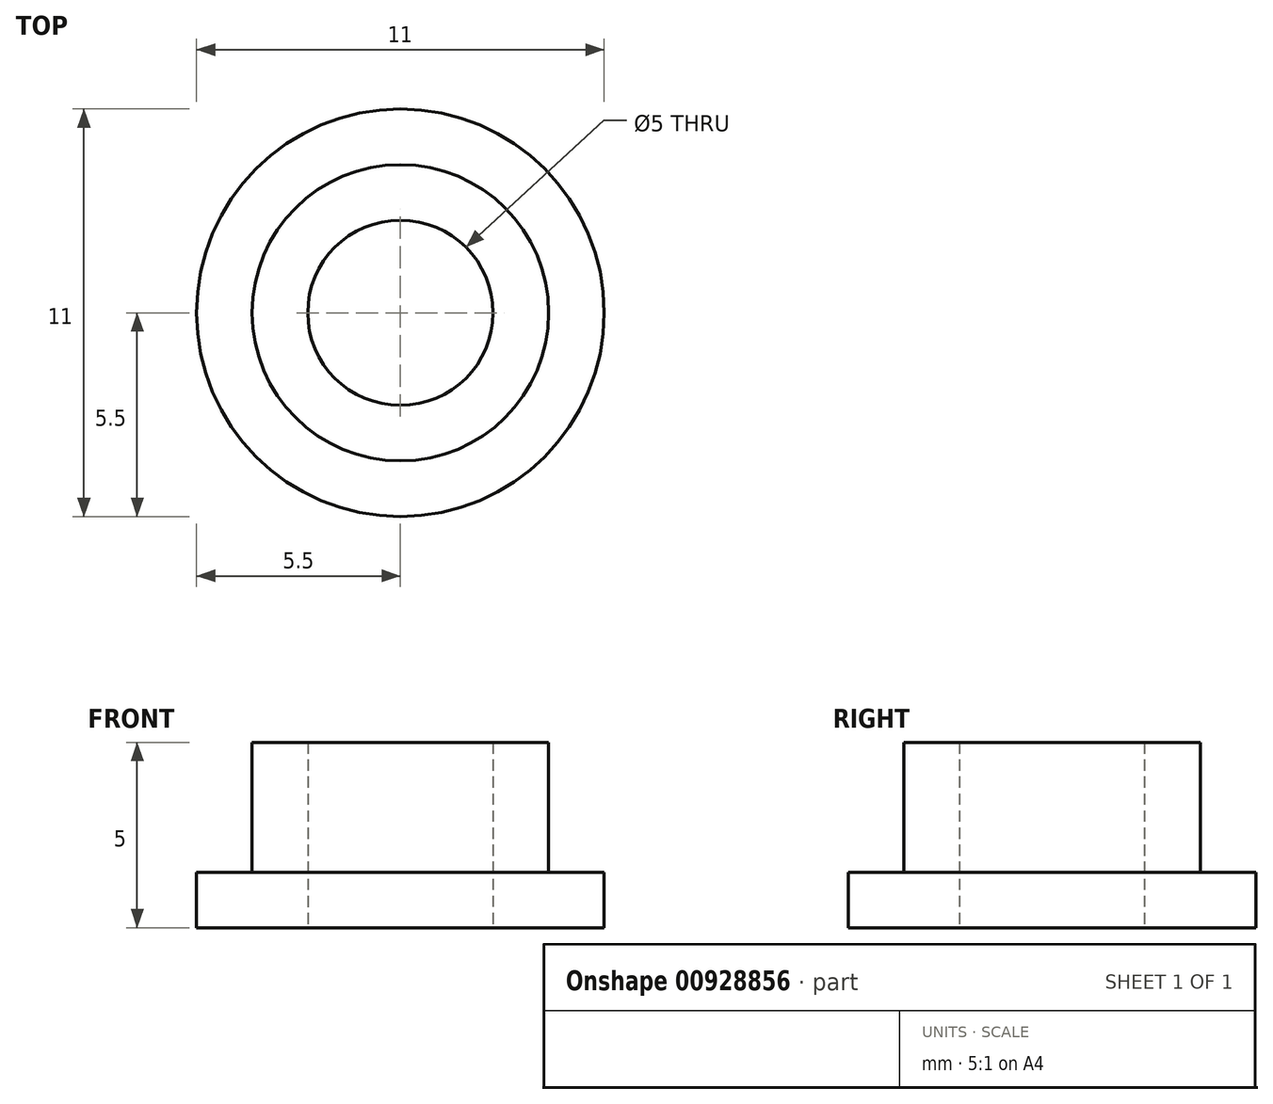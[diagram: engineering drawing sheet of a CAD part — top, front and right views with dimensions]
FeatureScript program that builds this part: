
annotation { "Feature Type Name" : "Feature", "Feature Type Description" : "" }
export const myFeature = defineFeature(function(context is Context, id is Id, definition is map)
    precondition{}
    {
        {
            var Q0;
            Q0=qCreatedBy(makeId("Front.planeOp"),FACE);
            var sketch = newSketch(context, id + "F0", { "sketchPlane" : qUnion([Q0])});
            skLineSegment(sketch, "E0", {"start": v(2.5, 5) * mm, "end": v(2.5, 0) * mm});
            skLineSegment(sketch, "E1", {"start": v(2.5, 0) * mm, "end": v(5.5, 0) * mm});
            skLineSegment(sketch, "E2", {"start": v(5.5, 0) * mm, "end": v(5.5, 1.5) * mm});
            skLineSegment(sketch, "E3", {"start": v(5.5, 1.5) * mm, "end": v(4, 1.5) * mm});
            skLineSegment(sketch, "E4", {"start": v(2.5, 5) * mm, "end": v(4, 5) * mm});
            skLineSegment(sketch, "E5", {"start": v(4, 5) * mm, "end": v(4, 1.5) * mm});
            skLineSegment(sketch, "E6", {"start": v(0, 0) * mm, "end": v(0, 6) * mm, "construction": true});
            skSolve(sketch);
        }
        {
            var Q0;
            Q0 = qSketchRegion(id + "F0", true);
            var Q1;
            Q1=sQuery(id+"F0.wireOp",EDGE,"E6");
            revolve(context, id + "F1", {"surfaceOperationType" : NewSurfaceOperationType.NEW, "entities" : qUnion([Q0]), "axis" : qUnion([Q1]), "revolveType" : RevolveType.FULL});
        }
    });
